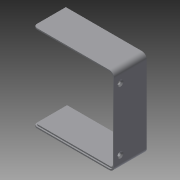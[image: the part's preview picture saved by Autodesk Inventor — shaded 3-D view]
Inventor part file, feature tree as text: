
AUTODESK INVENTOR PART (.ipt)
format: ipt  version: 2015 (Build 190159000, 159)  size: 151,552 bytes
history: native  units: in
note: dims shown in document units (in); Inventor stores cm internally (conversion verified against a paired STEP export)
features: other x3, reference x3, extrude x2, fillet x2, sketch x2, plane x1, chamfer x1
ambient origin geometry x8: Origin, YZ Plane, XZ Plane, XY Plane, X Axis, Y Axis, Z Axis, Center Point
bodies: Solid1 (feature_tree)
feature tree (14):
  plane  "Work Plane1"
  extrude  "Extrusion1"  Depth=0.0787in
  extrude  "Extrusion2"  Depth=0.9843in TaperAngle=0.0deg
  chamfer  "Chamfer1"  Distance=0.9843in
  other  "Lip1"
  other  "Lip4"
  other  "Lip5"
  fillet  "Fillet3"  Radius=0.0394in
  fillet  "Fillet4"  Radius=0.1181in
  sketch  "Sketch1"  dims[d0=0.0787in d1=0.0787in]
  reference  "Reference1"
  sketch  "Sketch2"  dims[d2=0.0787in d3=0.9843in d4=0.0in d5=0.9843in d6=0.0in d7=0.0394in d8=0.0787in d9=45.0deg d10=0.0394in d11=0.0394in d12=0.0in d13=0.0in d14=0.0in d15=0.0in d30=0.0394in d31=0.0394in d32=0.0in d33=0.0in d34=0.0in d35=0.0in d36=0.0394in d37=0.0394in d38=0.0in d39=0.0in d40=0.0in d41=0.0in d42=0.1181in d43=0.0787in]
  reference  "Reference2"
  reference  "Reference3"
